# Revit family: Sanitary_Taps-Mixers_hansgrohe_71472XXX-Vernis-Shape-Bath-mixer-set-for
name_source: partatom
category: Plumbing Fixtures
revit_build: Autodesk Revit 2018 (Build: 20190510_1515(x64)
units: mm (PartAtom-declared; Revit-internal decimal feet)

## family parameters
Always vertical = No
Cut with Voids When Loaded = No
OmniClass Number = 23.31.11.00
OmniClass Title = Faucets
Part Type = Normal
Room Calculation Point = No
Round Connector Dimension = Use Diameter
Shared = No
Work Plane-Based = Yes

## types (2) — shared parameters
Always visible = Yes
BIMobject category = Taps & Mixers
Default Elevation = 1219.2 mm  [stored 4 ft]
Description = Vernis Shape Bath mixer set for concealed installation
Design country = Germany
EAN code = 4059625399880
Edition number = 1
GTIN code = https://4059625399880
IFC Classification = Valve
Installation instructions = https://www.hansgrohe.com
Manufacturer = Hansgrohe
Manufacturer country = Germany
Manufacturer name = hansgrohe
Model = 71472XXX
Product Guid = e7ee82af-24c5-4cc3-89ea-989d8b88d344
Product SKU = 71472XXX
Product data url = https://bimobject.com
Product family = Vernis Shape
Product group = Bath mixers
Product name = 71472XXX Vernis Shape Bath mixer set for concealed installation
Product url = https://www.hansgrohe.com
QR code = https://bimobject.com
URL = https://www.hansgrohe.com
Weight Net (Kg) = 1,5

## per-type parameters (varying)
| type | Material |
| 000 Chrome | Hansgrohe - Metal - 000 Chrome |
| 670 Matte Black | Hansgrohe - Metal - 670 Matte Black |

note: [stored X ft] marks values corroborated as IEEE doubles in the binary element streams (Revit-internal decimal feet)

## geometry (parser evidence)
native form markers: Blend x5, Sweep x2
no freeform markers — native parametric forms only
